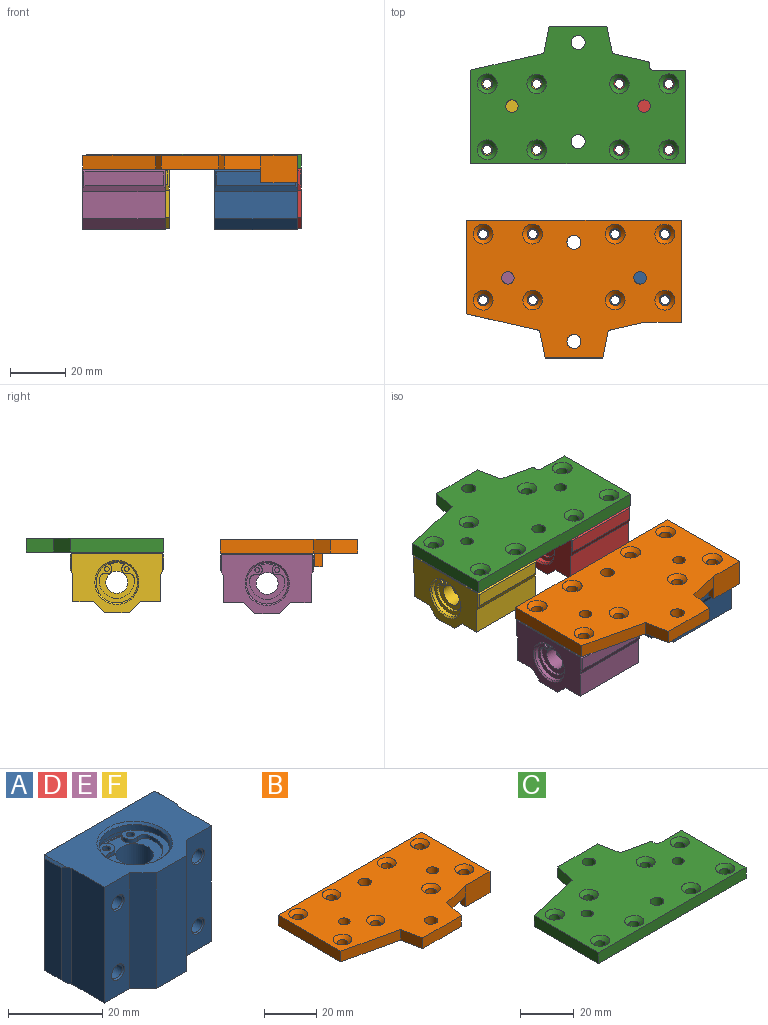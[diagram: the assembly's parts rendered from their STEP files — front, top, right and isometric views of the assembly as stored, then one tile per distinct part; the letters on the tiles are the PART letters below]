
ASSEMBLY  parts=6 mates=4
PART A: 101 faces, bbox 34x22x30 mm
  f0: cylinder r=7.5mm len=15mm, axis (0,0,-1), area 11.8mm2, adj f30,f89
  f1: plane 9.06x1.44mm, normal (0,0,-1), area 2.8mm2, adj f26,f27,f84,f85
  f2: plane 9.06x1.44mm, normal (0,0,1), area 2.8mm2, adj f31,f32,f70,f71
  f3: plane 30x7.5mm, normal (0,-1,0), area 201.6mm2, adj f7,f8,f11,f12,f52,f57
  f4: plane 29x8mm, normal (0,1,0), area 206.9mm2, adj f21,f22,f23,f24,f48,f53
  f5: plane 30x7.5mm, normal (0,-1,0), area 201.6mm2, adj f7,f8,f14,f15,f42,f47
  f6: plane 29x8mm, normal (0,1,0), area 206.9mm2, adj f18,f19,f23,f24,f38,f43
  f7: plane 33x21.5mm, normal (0,0,1), area 418mm2, adj f3,f5,f10,f11,f12,f13,f14,f15
  f8: plane 33x21.5mm, normal (0,0,-1), area 418mm2, adj f3,f5,f10,f11,f12,f13,f14,f15
  f9: plane 29x5mm, normal (-1,0,0), area 145mm2, adj f10,f22,f34,f35
  f10: plane 30x2.14mm, normal (-0.91,-0.42,0), area 70.4mm2, adj f7,f8,f9,f11,f34,f35
  f11: plane 30x9.86mm, normal (-1,0,0), area 295.7mm2, adj f3,f7,f8,f10
  f12: plane 30x4mm, normal (-0.71,-0.71,0), area 169.7mm2, adj f3,f7,f8,f13
  f13: plane 30x9mm, normal (0,-1,0), area 270mm2, adj f7,f8,f12,f14
  f14: plane 30x4mm, normal (0.71,-0.71,0), area 169.7mm2, adj f5,f7,f8,f13
  f15: plane 30x9.86mm, normal (1,0,0), area 295.7mm2, adj f5,f7,f8,f16
  f16: plane 30x2.14mm, normal (0.91,-0.42,0), area 70.4mm2, adj f7,f8,f15,f17,f36,f37
  f17: plane 29x5mm, normal (1,0,0), area 145mm2, adj f16,f18,f36,f37
  f18: plane 30x1mm, normal (0.71,0.71,0), area 41.7mm2, adj f6,f17,f23,f24,f36,f37
  f19: plane 29.8x0.4mm, normal (-0.71,0.71,0), area 16.6mm2, adj f6,f20,f23,f24
  f20: plane 29.8x15.2mm, normal (0,1,0), area 453mm2, adj f19,f21,f23,f24
  f21: plane 29.8x0.4mm, normal (0.71,0.71,0), area 16.6mm2, adj f4,f20,f23,f24
  f22: plane 30x1mm, normal (-0.71,0.71,0), area 41.7mm2, adj f4,f9,f23,f24,f34,f35
  f23: plane 33x0.5mm, normal (0,0.71,-0.71), area 14.2mm2, adj f4,f6,f8,f18,f19,f20,f21,f22
  f24: plane 33x0.5mm, normal (0,0.71,0.71), area 14.2mm2, adj f4,f6,f7,f18,f19,f20,f21,f22
  f25: cone r=8mm half-angle=45deg, axis (0,0,1), area 34.4mm2, adj f7,f26
  f26: cylinder r=7.5mm len=15mm, axis (0,0,-1), area 70.7mm2, adj f1,f25,f92
  f27: cylinder r=7.85mm len=15.7mm, axis (0,0,-1), area 17.1mm2, adj f1,f28,f84,f85,f86
  f28: plane 15.7x15.7mm, normal (0,0,1), area 16.9mm2, adj f27,f29
  f29: cylinder r=7.5mm len=15mm, axis (0,0,-1), area 11.8mm2, adj f28,f87
  f30: plane 15.7x15.7mm, normal (0,0,-1), area 16.9mm2, adj f0,f31
  f31: cylinder r=7.85mm len=15.7mm, axis (0,0,-1), area 17.1mm2, adj f2,f30,f70,f71,f72
  f32: cylinder r=7.5mm len=15mm, axis (0,0,-1), area 70.7mm2, adj f2,f33,f60
  f33: cone r=7.5mm half-angle=45deg, axis (0,0,-1), area 34.4mm2, adj f8,f32
  f34: plane 6.57x0.5mm, normal (-0.71,0,0.71), area 4.1mm2, adj f7,f9,f10,f22
  f35: plane 6.57x0.5mm, normal (-0.71,0,-0.71), area 4.1mm2, adj f8,f9,f10,f22
  f36: plane 6.57x0.5mm, normal (0.71,0,0.71), area 4.1mm2, adj f7,f16,f17,f18
  f37: plane 6.57x0.5mm, normal (0.71,0,-0.71), area 4.1mm2, adj f8,f16,f17,f18
  f38: cone r=2mm half-angle=45deg, axis (0,1,0), area 6.1mm2, adj f6,f39
  f39: cylinder r=1.62mm len=9.62mm, axis (0,-1,0), area 98mm2, adj f38,f40
  f40: plane 3.4x3.4mm, normal (0,-1,0), area 0.8mm2, adj f39,f41
  f41: cylinder r=1.7mm len=7.6mm, axis (0,-1,0), area 81.2mm2, adj f40,f42
  f42: cone r=1.7mm half-angle=30deg, axis (0,-1,0), area 5.3mm2, adj f5,f41
  f43: cone r=2mm half-angle=45deg, axis (0,1,0), area 6.1mm2, adj f6,f44
  f44: cylinder r=1.62mm len=9.62mm, axis (0,-1,0), area 98mm2, adj f43,f45
  f45: plane 3.4x3.4mm, normal (0,-1,0), area 0.8mm2, adj f44,f46
  f46: cylinder r=1.7mm len=7.6mm, axis (0,-1,0), area 81.2mm2, adj f45,f47
  f47: cone r=1.7mm half-angle=30deg, axis (0,-1,0), area 5.3mm2, adj f5,f46
  f48: cone r=2mm half-angle=45deg, axis (0,1,0), area 6.1mm2, adj f4,f49
  f49: cylinder r=1.62mm len=9.62mm, axis (0,-1,0), area 98mm2, adj f48,f50
  f50: plane 3.4x3.4mm, normal (0,-1,0), area 0.8mm2, adj f49,f51
  f51: cylinder r=1.7mm len=7.6mm, axis (0,-1,0), area 81.2mm2, adj f50,f52
  f52: cone r=1.7mm half-angle=30deg, axis (0,-1,0), area 5.3mm2, adj f3,f51
  f53: cone r=2mm half-angle=45deg, axis (0,1,0), area 6.1mm2, adj f4,f54
  f54: cylinder r=1.62mm len=9.62mm, axis (0,-1,0), area 98mm2, adj f53,f55
  f55: plane 3.4x3.4mm, normal (0,-1,0), area 0.8mm2, adj f54,f56
  f56: cylinder r=1.7mm len=7.6mm, axis (0,-1,0), area 81.2mm2, adj f55,f57
  f57: cone r=1.7mm half-angle=30deg, axis (0,-1,0), area 5.3mm2, adj f3,f56
  f58: plane 1.7x1.7mm, normal (0,0,-1), area 2.3mm2, adj f62
  f59: plane 1.7x1.7mm, normal (0,0,-1), area 2.3mm2, adj f63
  f60: plane 15x14.21mm, normal (0,0,-1), area 58.1mm2, adj f32,f61,f62,f63,f64,f65,f66,f67
  f61: plane 1x0.13mm, normal (0.94,0.33,0), area 0.1mm2, adj f60,f64,f71,f91
  f62: cylinder r=0.85mm len=1.7mm, axis (0,0,-1), area 5.3mm2, adj f58,f60
  f63: cylinder r=0.85mm len=1.7mm, axis (0,0,-1), area 5.3mm2, adj f59,f60
  f64: cylinder r=1.8mm len=2.39mm, axis (0,0,-1), area 3.9mm2, adj f60,f61,f65,f91
  f65: cylinder r=1.8mm len=2.2mm, axis (0,0,-1), area 2.9mm2, adj f60,f64,f66,f91
  f66: cylinder r=6.35mm len=12.7mm, axis (0,0,-1), area 22.4mm2, adj f60,f65,f67,f91
  f67: cylinder r=1.8mm len=2.2mm, axis (0,0,-1), area 2.9mm2, adj f60,f66,f68,f91
  f68: cylinder r=1.8mm len=2.39mm, axis (0,0,-1), area 3.9mm2, adj f60,f67,f69,f91
  f69: plane 1x0.13mm, normal (-0.94,0.33,0), area 0.1mm2, adj f60,f68,f70,f91
  f70: cylinder r=1.7mm len=2.59mm, axis (0,0,-1), area 3.1mm2, adj f2,f31,f60,f69,f72,f91
  f71: cylinder r=1.7mm len=2.59mm, axis (0,0,-1), area 3.1mm2, adj f2,f31,f60,f61,f72,f91
  f72: plane 15.7x14.57mm, normal (0,0,1), area 30mm2, adj f31,f70,f71,f89
  f73: plane 1.7x1.7mm, normal (0,0,1), area 2.3mm2, adj f76
  f74: plane 1.7x1.7mm, normal (0,0,1), area 2.3mm2, adj f77
  f75: plane 1x0.13mm, normal (-0.94,0.33,0), area 0.1mm2, adj f78,f85,f90,f92
  f76: cylinder r=0.85mm len=1.7mm, axis (0,0,1), area 5.3mm2, adj f73,f92
  f77: cylinder r=0.85mm len=1.7mm, axis (0,0,1), area 5.3mm2, adj f74,f92
  f78: cylinder r=1.8mm len=2.39mm, axis (0,0,1), area 3.9mm2, adj f75,f79,f90,f92
  f79: cylinder r=1.8mm len=2.2mm, axis (0,0,1), area 2.9mm2, adj f78,f80,f90,f92
  f80: cylinder r=6.35mm len=12.7mm, axis (0,0,1), area 22.4mm2, adj f79,f81,f90,f92
  f81: cylinder r=1.8mm len=2.2mm, axis (0,0,1), area 2.9mm2, adj f80,f82,f90,f92
  f82: cylinder r=1.8mm len=2.39mm, axis (0,0,1), area 3.9mm2, adj f81,f83,f90,f92
  f83: plane 1x0.13mm, normal (0.94,0.33,0), area 0.1mm2, adj f82,f84,f90,f92
  f84: cylinder r=1.7mm len=2.59mm, axis (0,0,1), area 3.1mm2, adj f1,f27,f83,f86,f90,f92
  f85: cylinder r=1.7mm len=2.59mm, axis (0,0,1), area 3.1mm2, adj f1,f27,f75,f86,f90,f92
  f86: plane 15.7x14.57mm, normal (0,0,-1), area 30mm2, adj f27,f84,f85,f87
  f87: torus R=7.1mm, axis (0,0,1), area 29mm2, adj f29,f86,f90
  f88: cylinder r=4mm len=24mm, axis (0,0,1), area 603.2mm2, adj f90,f91
  f89: torus R=7.1mm, axis (0,0,1), area 29mm2, adj f0,f72,f91
  f90: plane 12.95x12.7mm, normal (0,0,1), area 61.3mm2, adj f75,f78,f79,f80,f81,f82,f83,f84
  f91: plane 12.95x12.7mm, normal (0,0,-1), area 61.3mm2, adj f61,f64,f65,f66,f67,f68,f69,f70
  f92: plane 15x14.21mm, normal (0,0,1), area 58.1mm2, adj f26,f75,f76,f77,f78,f79,f80,f81
  f93: plane 15x15mm, normal (0,0,-1), area 16.1mm2, adj f94,f96
  f94: cylinder r=7.15mm len=14.3mm, axis (0,0,1), area 49.4mm2, adj f93,f95
  f95: plane 15x15mm, normal (0,0,1), area 16.1mm2, adj f94,f96
  f96: cylinder r=7.5mm len=15mm, axis (0,0,-1), area 51.8mm2, adj f93,f95
  f97: plane 15x15mm, normal (0,0,-1), area 16.1mm2, adj f98,f100
  f98: cylinder r=7.15mm len=14.3mm, axis (0,0,1), area 49.4mm2, adj f97,f99
  f99: plane 15x15mm, normal (0,0,1), area 16.1mm2, adj f98,f100
  f100: cylinder r=7.5mm len=15mm, axis (0,0,-1), area 51.8mm2, adj f97,f99
PART B: 34 faces, bbox 78x50x10 mm
  f0: plane 13.25x5mm, normal (0.22,-0.98,0), area 67.9mm2, adj f2,f20,f21,f30
  f1: plane 37x10mm, normal (1,0,0), area 199mm2, adj f7,f20,f21,f30,f32,f33
  f2: plane 10x5mm, normal (0.98,-0.2,0), area 51mm2, adj f0,f3,f20,f21
  f3: plane 21x5mm, normal (0,-1,0), area 105mm2, adj f2,f4,f20,f21
  f4: plane 10x5mm, normal (-0.98,-0.2,0), area 51mm2, adj f3,f5,f20,f21
  f5: plane 26.5x6mm, normal (-0.22,-0.98,0), area 135.9mm2, adj f4,f6,f20,f21
  f6: plane 34x5mm, normal (-1,0,0), area 170mm2, adj f5,f7,f20,f21
  f7: plane 78x5mm, normal (0,1,0), area 390mm2, adj f1,f6,f20,f21
  f8: cylinder r=2.1mm len=4.2mm, axis (0,0,-1), area 46.2mm2, adj f21,f22
  f9: cylinder r=2.1mm len=4.2mm, axis (0,0,-1), area 46.2mm2, adj f21,f24
  f10: cylinder r=2.1mm len=4.2mm, axis (0,0,-1), area 46.2mm2, adj f21,f29
  f11: cylinder r=2.1mm len=4.2mm, axis (0,0,-1), area 46.2mm2, adj f21,f28
  f12: cylinder r=2.05mm len=4.1mm, axis (0,0,-1), area 45.1mm2, adj f21,f26
  f13: cylinder r=2.1mm len=4.2mm, axis (0,0,-1), area 46.2mm2, adj f21,f27
  f14: cylinder r=2.05mm len=4.1mm, axis (0,0,-1), area 45.1mm2, adj f21,f23
  f15: cylinder r=2.1mm len=4.2mm, axis (0,0,-1), area 46.2mm2, adj f21,f25
  f16: cylinder r=2.55mm len=5.1mm, axis (0,0,-1), area 80.1mm2, adj f20,f21
  f17: cylinder r=2.25mm len=5mm, axis (0,0,-1), area 70.7mm2, adj f20,f21
  f18: cylinder r=2.25mm len=5mm, axis (0,0,-1), area 70.7mm2, adj f20,f21
  f19: cylinder r=2.55mm len=5.1mm, axis (0,0,-1), area 80.1mm2, adj f20,f21
  f20: plane 78x50mm, normal (0,0,1), area 2814.7mm2, adj f0,f1,f2,f3,f4,f5,f6,f7
  f21: plane 78x50mm, normal (0,0,-1), area 2991.6mm2, adj f0,f1,f2,f3,f4,f5,f6,f7
  f22: cone r=2.1mm half-angle=45deg, axis (0,0,1), area 38mm2, adj f8,f20
  f23: cone r=2.05mm half-angle=45deg, axis (0,0,1), area 37.3mm2, adj f14,f20
  f24: cone r=2.1mm half-angle=45deg, axis (0,0,1), area 38mm2, adj f9,f20
  f25: cone r=2.1mm half-angle=45deg, axis (0,0,1), area 38mm2, adj f15,f20
  f26: cone r=2.05mm half-angle=45deg, axis (0,0,1), area 37.3mm2, adj f12,f20
  f27: cone r=2.1mm half-angle=45deg, axis (0,0,1), area 38mm2, adj f13,f20
  f28: cone r=2.1mm half-angle=45deg, axis (0,0,1), area 38mm2, adj f11,f20
  f29: cone r=2.1mm half-angle=45deg, axis (0,0,1), area 38mm2, adj f10,f20
  f30: plane 13.25x10mm, normal (0,-1,0), area 132.5mm2, adj f0,f1,f20,f31,f33
  f31: plane 5x2.8mm, normal (-1,0,0), area 14mm2, adj f21,f30,f32,f33
  f32: plane 13.25x5mm, normal (0,1,0), area 66.3mm2, adj f1,f21,f31,f33
  f33: plane 13.25x2.8mm, normal (0,0,-1), area 37.1mm2, adj f1,f30,f31,f32
PART C: 34 faces, bbox 78x50x5 mm
  f0: plane 78x50mm, normal (0,0,1), area 2775.8mm2, adj f1,f2,f3,f4,f5,f6,f7,f8
  f1: plane 34x5mm, normal (1,0,0), area 170mm2, adj f0,f8,f21,f31
  f2: plane 12.72x5mm, normal (0.22,0.98,0), area 65.2mm2, adj f0,f3,f21,f33
  f3: plane 10x5mm, normal (0.98,0.2,0), area 51mm2, adj f0,f2,f4,f21
  f4: plane 21x5mm, normal (0,1,0), area 105mm2, adj f0,f3,f5,f21
  f5: plane 10x5mm, normal (-0.98,0.2,0), area 51mm2, adj f0,f4,f6,f21
  f6: plane 26.5x6mm, normal (-0.22,0.98,0), area 135.9mm2, adj f0,f5,f7,f21
  f7: plane 34x5mm, normal (-1,0,0), area 170mm2, adj f0,f6,f8,f21
  f8: plane 78x5mm, normal (0,-1,0), area 390mm2, adj f0,f1,f7,f21
  f9: cylinder r=2.1mm len=4.2mm, axis (0,0,-1), area 46.2mm2, adj f21,f22
  f10: cylinder r=2.1mm len=4.2mm, axis (0,0,-1), area 46.2mm2, adj f21,f24
  f11: cylinder r=2.1mm len=4.2mm, axis (0,0,-1), area 46.2mm2, adj f21,f29
  f12: cylinder r=2.1mm len=4.2mm, axis (0,0,-1), area 46.2mm2, adj f21,f28
  f13: cylinder r=2.05mm len=4.1mm, axis (0,0,-1), area 45.1mm2, adj f21,f26
  f14: cylinder r=2.1mm len=4.2mm, axis (0,0,-1), area 46.2mm2, adj f21,f27
  f15: cylinder r=2.05mm len=4.1mm, axis (0,0,-1), area 45.1mm2, adj f21,f23
  f16: cylinder r=2.1mm len=4.2mm, axis (0,0,-1), area 46.2mm2, adj f21,f25
  f17: cylinder r=2.55mm len=5.1mm, axis (0,0,-1), area 80.1mm2, adj f0,f21
  f18: cylinder r=2.25mm len=5mm, axis (0,0,-1), area 70.7mm2, adj f0,f21
  f19: cylinder r=2.25mm len=5mm, axis (0,0,-1), area 70.7mm2, adj f0,f21
  f20: cylinder r=2.55mm len=5.1mm, axis (0,0,-1), area 80.1mm2, adj f0,f21
  f21: plane 78x50mm, normal (0,0,-1), area 2989.8mm2, adj f1,f2,f3,f4,f5,f6,f7,f8
  f22: cone r=2.1mm half-angle=45deg, axis (0,0,1), area 38mm2, adj f0,f9
  f23: cone r=2.05mm half-angle=45deg, axis (0,0,1), area 37.3mm2, adj f0,f15
  f24: cone r=2.1mm half-angle=45deg, axis (0,0,1), area 38mm2, adj f0,f10
  f25: cone r=2.1mm half-angle=45deg, axis (0,0,1), area 38mm2, adj f0,f16
  f26: cone r=2.05mm half-angle=45deg, axis (0,0,1), area 37.3mm2, adj f0,f13
  f27: cone r=2.1mm half-angle=45deg, axis (0,0,1), area 38mm2, adj f0,f14
  f28: cone r=2.1mm half-angle=45deg, axis (0,0,1), area 38mm2, adj f0,f12
  f29: cone r=2.1mm half-angle=45deg, axis (0,0,1), area 38mm2, adj f0,f11
  f30: plane 5x1.14mm, normal (1,0,0), area 5.7mm2, adj f0,f21,f32,f33
  f31: plane 12x5mm, normal (0,1,0), area 60mm2, adj f0,f1,f21,f32
  f32: cylinder r=1mm len=5mm, axis (0,0,-1), area 7.9mm2, adj f0,f21,f30,f31
  f33: cylinder r=1mm len=5mm, axis (0,0,1), area 6.7mm2, adj f0,f2,f21,f30
PART D: same geometry as A
PART E: same geometry as A
PART F: same geometry as A
PLACE A rot(axis=(0.58,0.58,0.58),120deg) t=(7.52,-54.61,-11.38)mm
PLACE B t=(-1.48,-20.61,-0.38)mm
PLACE C at identity fixed
PLACE D rot(axis=(0.58,0.58,0.58),120deg) t=(9,0,-11)mm
PLACE E rot(axis=(0.58,0.58,0.58),120deg) t=(-40.48,-54.61,-11.38)mm
PLACE F rot(axis=(0.58,0.58,0.58),120deg) t=(-39,0,-11)mm
MATE fastened A.f53 <-> B.f8  axis (0,0,1) through (31.52,-66.61,-0.38)mm
MATE fastened E.f48 <-> B.f11  axis (0,0,1) through (-34.48,-66.61,-0.38)mm
MATE fastened F.f53 <-> C.f14  axis (0,0,1) through (-15,-12,0)mm
MATE fastened D.f53 <-> C.f10  axis (0,0,1) through (33,-12,0)mm
